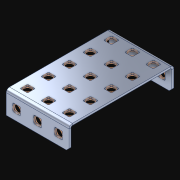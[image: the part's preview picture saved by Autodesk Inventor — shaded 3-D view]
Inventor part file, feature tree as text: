
AUTODESK INVENTOR PART (.ipt)
format: ipt  version: 2021 (Build 250183000, 183)  size: 1,393,664 bytes
history: native  units: in
note: dims shown in document units (in); Inventor stores cm internally (conversion verified against a paired STEP export)
features: extrude x22, other x22, sketch x4, pattern_linear x3
ambient origin geometry x8: Origin, YZ Plane, XZ Plane, XY Plane, X Axis, Y Axis, Z Axis, Center Point
bodies: Solid1 (feature_tree)
feature tree (51):
  pattern_linear  "Rectangular Pattern1"  Spacing1=0.182in  [1 undecoded]
  pattern_linear  "Rectangular Pattern2"  Spacing1=0.046in  [1 undecoded]
  pattern_linear  "Rectangular Pattern3"  Spacing1=0.5in  [1 undecoded]
  extrude  "Extrusion1"  Depth=0.5in
  sketch  "Sketch1"  dims[d0=0.182in]
  other  "Srf1"
  sketch  "Sketch2"  dims[d1=0.046in d2=0.0in]
  other  "Srf2"
  sketch  "Sketch3"  dims[d3=0.182in]
  other  "Srf3"
  other  "Srf4"
  other  "Srf5"
  other  "Srf38"
  other  "Srf39"
  other  "Srf72"
  other  "Srf73"
  other  "Srf74"
  other  "Srf107"
  other  "Srf108"
  other  "Srf109"
  other  "Srf142"
  other  "Srf143"
  other  "Srf144"
  other  "Srf177"
  other  "Srf178"
  other  "Srf179"
  other  "Srf212"
  other  "Srf213"
  sketch  "Sketch4"  dims[d4=0.046in d5=0.0in d6=0.182in d7=0.046in d8=0.0in d11=0.5in d12=1.1811in d14=0.5in d15=1.9685in d17=0.5in d18=1.1811in d20=0.5in d21=16.0in d22=0.0in]
  parser-record x1  (decoder bookkeeping rows leaked as tree rows — omitted from the tree; the rows remain in map.json)
  extrude  "ExtrusionSrf1"  Depth=0.5in
  extrude  "ExtrusionSrf2"  Depth=0.5in
  extrude  "ExtrusionSrf3"  Depth=0.5in
  extrude  "ExtrusionSrf4"  Depth=0.5in
  extrude  "ExtrusionSrf5"  Depth=0.5in
  extrude  "ExtrusionSrf38"  TaperAngle=0.0deg  [1 undecoded]
  extrude  "ExtrusionSrf39"  [1 undecoded]
  extrude  "ExtrusionSrf72"  [1 undecoded]
  extrude  "ExtrusionSrf73"  [1 undecoded]
  extrude  "ExtrusionSrf74"  [1 undecoded]
  extrude  "ExtrusionSrf107"  [1 undecoded]
  extrude  "ExtrusionSrf108"  [1 undecoded]
  extrude  "ExtrusionSrf109"  [1 undecoded]
  extrude  "ExtrusionSrf142"  [1 undecoded]
  extrude  "ExtrusionSrf143"  [1 undecoded]
  extrude  "ExtrusionSrf144"  [1 undecoded]
  extrude  "ExtrusionSrf177"  [1 undecoded]
  extrude  "ExtrusionSrf178"  [1 undecoded]
  extrude  "ExtrusionSrf179"  [1 undecoded]
  extrude  "ExtrusionSrf212"  [1 undecoded]
  extrude  "ExtrusionSrf213"  [1 undecoded]
note: 19 required parameter values undecoded (feature->parameter linkage not recoverable at this tier; creation-order binding heuristic only, values carry confidence <= 0.55)
